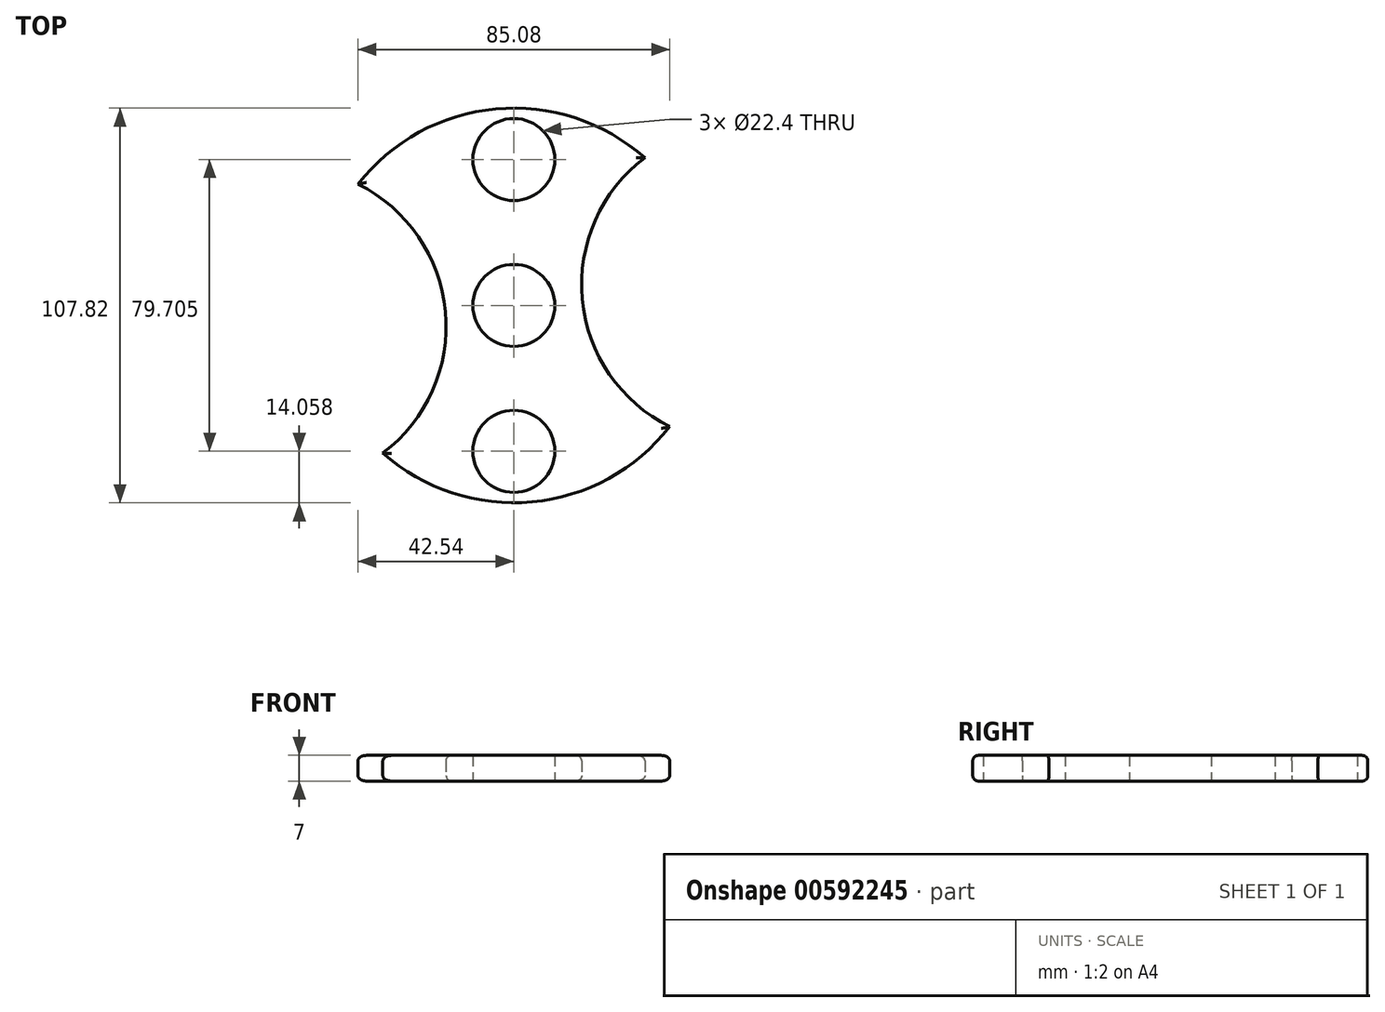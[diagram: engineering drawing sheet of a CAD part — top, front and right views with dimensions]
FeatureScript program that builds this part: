
annotation { "Feature Type Name" : "Feature", "Feature Type Description" : "" }
export const myFeature = defineFeature(function(context is Context, id is Id, definition is map)
    precondition{}
    {
        {
            var Q0;
            Q0=qCreatedBy(makeId("Top.planeOp"),FACE);
            var sketch = newSketch(context, id + "F0", { "sketchPlane" : qUnion([Q0])});
            skCircle(sketch, "E0", {"center": v(0, 0) * mm, "radius": 11.2 * mm});
            skCircle(sketch, "E1", {"center": v(0, 39.85) * mm, "radius": 11.2 * mm});
            skCircle(sketch, "E2.1.0", {"center": v(0, -39.85) * mm, "radius": 11.2 * mm});
            skArc(sketch, "E3", {"start": v(-35.77, -40.34) * mm, "mid": v(4.95, -53.68) * mm, "end": v(42.54, -33.11) * mm});
            skArc(sketch, "E4", {"start": v(-35.77, -40.34) * mm, "mid": v(-18.68, -1.72) * mm, "end": v(-42.54, 33.11) * mm});
            skArc(sketch, "E5.1.0", {"start": v(35.77, 40.34) * mm, "mid": v(18.68, 1.72) * mm, "end": v(42.54, -33.11) * mm});
            skArc(sketch, "E6.trimOffspring", {"start": v(35.77, 40.34) * mm, "mid": v(-4.95, 53.68) * mm, "end": v(-42.54, 33.11) * mm});
            skSolve(sketch);
        }
        {
            var Q0;
            Q0 = qSketchRegion(id + "F0", true);
            extrude(context, id + "F1", {"entities" : qUnion([Q0]), "depth" : 7 * mm, "offsetDistance" : 25 * mm});
        }
        {
            var Q0;
            Q0=makeQuery(id+"F1.opExtrude","CAP_EDGE",EDGE,{"disambiguationData":[OSD([sQuery(id+"F0.wireOp",EDGE,"E5.1.0")])],"isStart":false});
            var Q1;
            Q1=makeQuery(id+"F1.opExtrude","CAP_EDGE",EDGE,{"disambiguationData":[OSD([sQuery(id+"F0.wireOp",EDGE,"E3")])],"isStart":false});
            var Q2;
            Q2=makeQuery(id+"F1.opExtrude","CAP_EDGE",EDGE,{"disambiguationData":[OSD([sQuery(id+"F0.wireOp",EDGE,"E4")])],"isStart":false});
            var Q3;
            Q3=makeQuery(id+"F1.opExtrude","CAP_EDGE",EDGE,{"disambiguationData":[OSD([sQuery(id+"F0.wireOp",EDGE,"E6.trimOffspring")])],"isStart":false});
            fillet(context, id + "F2", {"entities" : qUnion([Q0, Q1, Q2, Q3]), "radius" : 1.5 * mm, "tangentPropagation" : true, "allowEdgeOverflow" : false});
        }
        {
            var Q0;
            Q0=makeQuery(id+"F1.opExtrude","CAP_EDGE",EDGE,{"disambiguationData":[OSD([sQuery(id+"F0.wireOp",EDGE,"E3")])],"isStart":true});
            var Q1;
            Q1=makeQuery(id+"F1.opExtrude","CAP_EDGE",EDGE,{"disambiguationData":[OSD([sQuery(id+"F0.wireOp",EDGE,"E5.1.0")])],"isStart":true});
            var Q2;
            Q2=makeQuery(id+"F1.opExtrude","CAP_EDGE",EDGE,{"disambiguationData":[OSD([sQuery(id+"F0.wireOp",EDGE,"E6.trimOffspring")])],"isStart":true});
            var Q3;
            Q3=makeQuery(id+"F1.opExtrude","CAP_EDGE",EDGE,{"disambiguationData":[OSD([sQuery(id+"F0.wireOp",EDGE,"E4")])],"isStart":true});
            fillet(context, id + "F3", {"entities" : qUnion([Q0, Q1, Q2, Q3]), "radius" : 1.5 * mm, "tangentPropagation" : true, "allowEdgeOverflow" : false});
        }
    });
